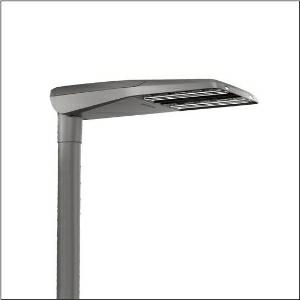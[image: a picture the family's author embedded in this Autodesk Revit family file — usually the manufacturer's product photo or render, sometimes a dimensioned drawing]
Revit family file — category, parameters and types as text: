
# Revit family: streetlight_sl_11_iq_midi___st1_2a_5xc3a51f08le_94b4
name_source: partatom
category: Lighting Fixtures
units: mm (PartAtom-declared; Revit-internal decimal feet)

## family parameters
Cut with Voids When Loaded = No
Host = Face
Light Source = No
Part Type = Normal
Room Calculation Point = No
Round Connector Dimension = Use Diameter
Shared = No

## types (1)
- --- (1 x LED, 9210 lm, 60.4 W, 3000K)
    Apparent Load = 60 VA
    CIE Flux Codes = 32 70 96 100 100
    Color Rendering = 70
    Color Temperature = 3000K
    Default Elevation = 1800 mm
    Description = Streetlight SL 11 iQ midi, mast luminaire, primary light control with 3 zone facetted reflector, of plastic, silver coated, highly specular, primary optical cover: cover, of PMMA, transparent, light distribution: ST1.2a, light emission: direct distribution, primary light characteristic: asymmetric, installation type: post-top, side-entry, lamps: LED, High Power LED, rated values: 9.210lm | 60,4W | 152,5lm/W (begin service life); end service life: 9.210lm | 62,5W; at 50% lumin. flux: 4.605lm | 29,6W | 155,6lm/W, colour temperature: 3000K, colour rendering: CRI > 70, light colour: 730, light setting 1 begin service life: 100% | 9.210lm | 60,4W | 152,5lm/W | 3.000K, light setting 1 end service life: 62,5W, further light settings possible, control: Street-Remote, optimised constant luminous flux control (CLO 2.0), Desk-Remote (wireless, voltage-free reading and setting of iQ features in the workshop via application-optimized NFC function/RFID function), Light-Fading, Smart-Wire, Night-Set, Lumen-Switch, Temp-Guard, Auto-Match, with cable H07RN-F 5x 1.5mm², mains connection: 230..240V, AC, 50/60Hz, connection cable pre-assembled, cable length: 8,5m, luminaire housing, of diecast aluminium, powder-coated, Siteco® metallic grey (DB 702S), please order mast flange separately, inclination adjustable without tools: 0°, 5°, 10°, 15° (post-top) | 0°, -5°, -10°, -15° (side-entry), sealing non-destructively replaceable, multi-level sealing system, length: 780mm, width: 376mm, height: 118mm, mast flange for spigot size: 42mm (side-entry): 5XC10008XM4, 60/48mm (side-entry/post-top): 5XC10108XM2, 76/60mm (side-entry/post-top): 5XC10108XM1, equipment: standard, protection rating (complete): IP66, insulation class (complete): insulation class II (safety insulation), certification: CE, ENEC, ENEC+, VDE, impact resistance: IK10, permissible operating ambient temperature for outdoor applications: -25..+50°C, standard-compliant lighting for roads and squares, Environmental Product Declaration (EPD) tested and certified by an independent institute, packaging unit: 1 piece

Light Distribution: ST1.2a
    Height = 118 mm
    Lamp = 1 x LED
    Lamp Light Flux = 9210 lm
    Lamp Power = 60.4 W
    Lamp count = 1
    Length = 780 mm
    Luminous efficacy = 152 lm/W
    Manufacturer = Siteco
    ModVariant = No
    Model = 5XC3A51F08LE
    Number of Poles = 1
    OnlyDefault = Yes
    Power Factor = 1
    Product Name = Streetlight SL 11 iQ midi | ST1.2a
    Product group = mast luminaire | pylon top
    ProductGroupID = 6100
    Protection Class = Protection class II
    Protection Degree = IP 66
    RLX_Detail_Level = 1
    RLX_Emergency_Light_Flux = 0 lm
    RLX_Emergency_Type = 0
    RLX_Emergency_Type_DB = No
    RlxData = <blob elided: 70721 chars, md5=eb5aeb7d>
    Socket = socket
    Standby Power = 0 W
    System Light Flux = 9210 lm
    System Power = 60 W
    Type Comments = factory setting: luminous flux: 100 % | dim-lin: 254 | 520 mA
    Type Image = l_1005960.jpg
    URL = http://relux.com
    VarID = @adj_218241
    Voltage = 0 V
    Weight = 0.00 kg
    Width = 376 mm

## geometry (parser evidence)
native form markers: Blend x4, Sweep x8
no freeform markers — native parametric forms only
